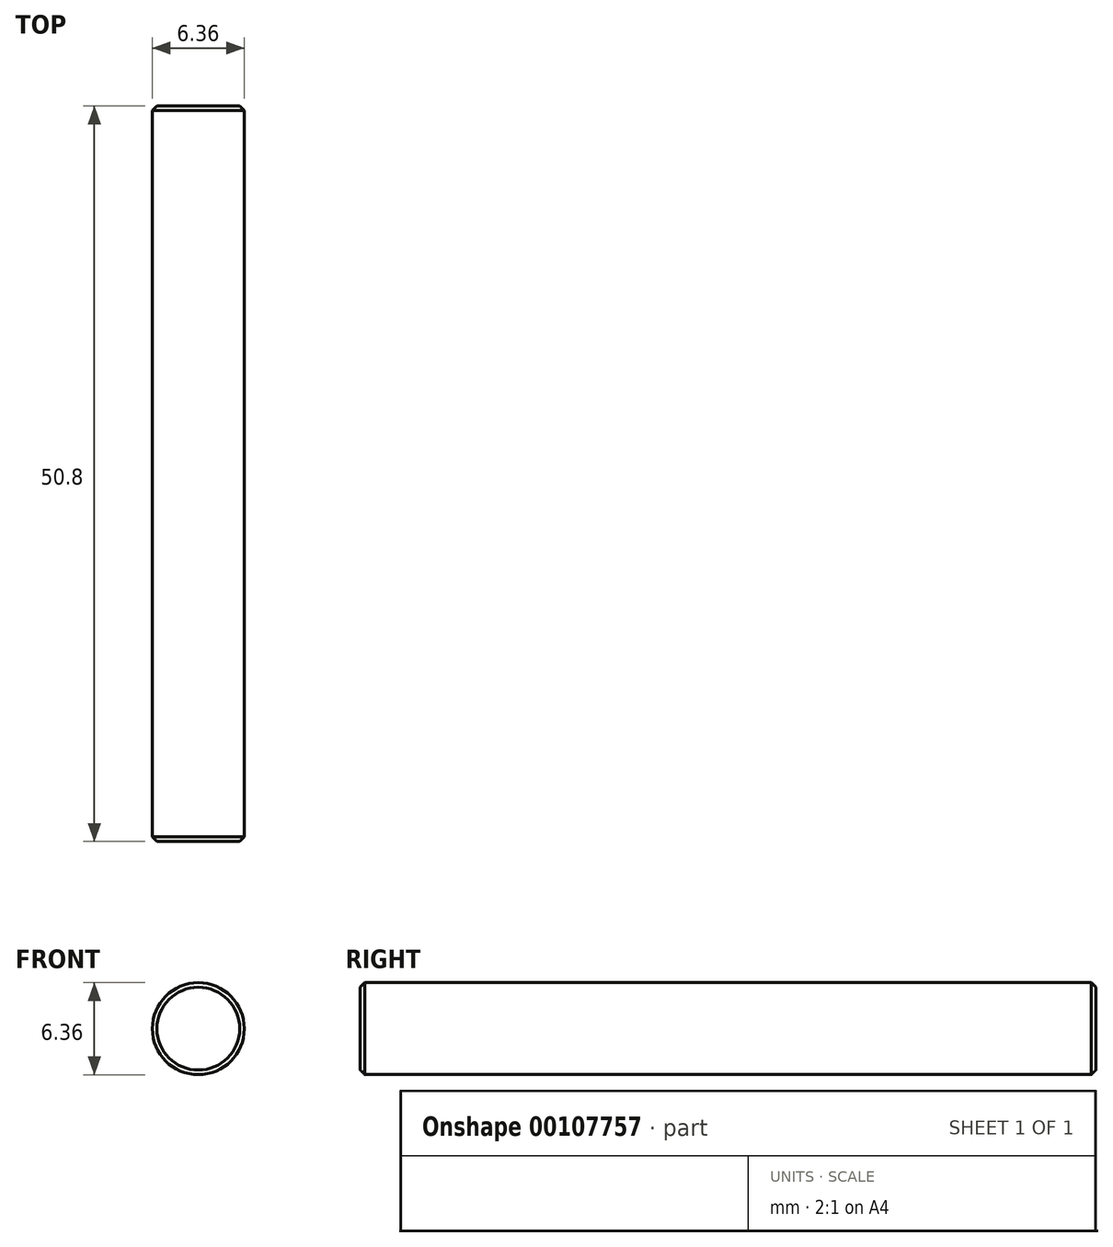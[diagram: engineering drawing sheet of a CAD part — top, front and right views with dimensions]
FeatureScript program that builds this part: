
annotation { "Feature Type Name" : "Feature", "Feature Type Description" : "" }
export const myFeature = defineFeature(function(context is Context, id is Id, definition is map)
    precondition{}
    {
        {
            var Q0;
            Q0=qCreatedBy(makeId("Front.planeOp"),FACE);
            var sketch = newSketch(context, id + "F0", { "sketchPlane" : qUnion([Q0])});
            skCircle(sketch, "E0", {"center": v(0, 0) * mm, "radius": 3.18 * mm});
            skSolve(sketch);
        }
        {
            var Q0;
            Q0 = qSketchRegion(id + "F0", true);
            extrude(context, id + "F1", {"entities" : qUnion([Q0]), "depth" : 50.8 * mm});
        }
        {
            var Q0;
            Q0=makeQuery(id+"F1.opExtrude","CAP_EDGE",EDGE,{"disambiguationData":[OSD([sQuery(id+"F0.wireOp",EDGE,"E0")])],"isStart":true});
            var Q1;
            Q1=makeQuery(id+"F1.opExtrude","CAP_EDGE",EDGE,{"disambiguationData":[OSD([sQuery(id+"F0.wireOp",EDGE,"E0")])],"isStart":false});
            chamfer(context, id + "F2", {"entities" : qUnion([Q0, Q1]), "width" : 0.32 * mm, "tangentPropagation" : true});
        }
    });
